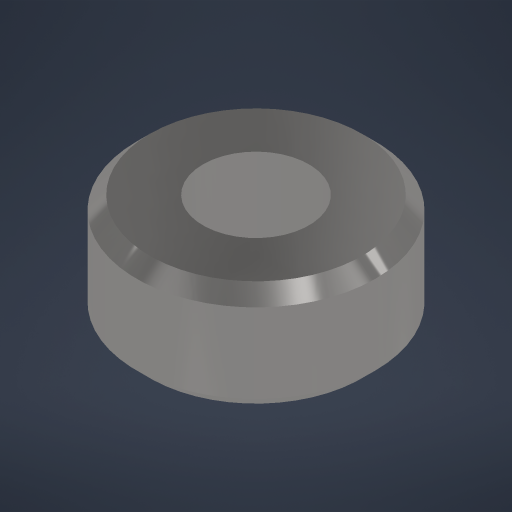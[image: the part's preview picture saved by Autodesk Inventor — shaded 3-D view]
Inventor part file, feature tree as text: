
AUTODESK INVENTOR PART (.ipt)
format: ipt  version: 2024 (Build 280153000, 153)  size: 181,248 bytes
history: native  units: in
note: dims shown in document units (in); Inventor stores cm internally (conversion verified against a paired STEP export)
features: extrude x1, chamfer x1, sketch x1
ambient origin geometry x8: Origin, YZ Plane, XZ Plane, XY Plane, X Axis, Y Axis, Z Axis, Center Point
bodies: Solid1 (feature_tree)
feature tree (3):
  extrude  "Extrusion1"  Depth=0.0787in
  chamfer  "Chamfer1"  Distance=0.1575in
  sketch  "Sketch1"  dims[d0=0.1575in d1=0.3543in d2=0.1575in d3=0.0in d4=0.0197in d5=0.0787in d6=45.0deg]
